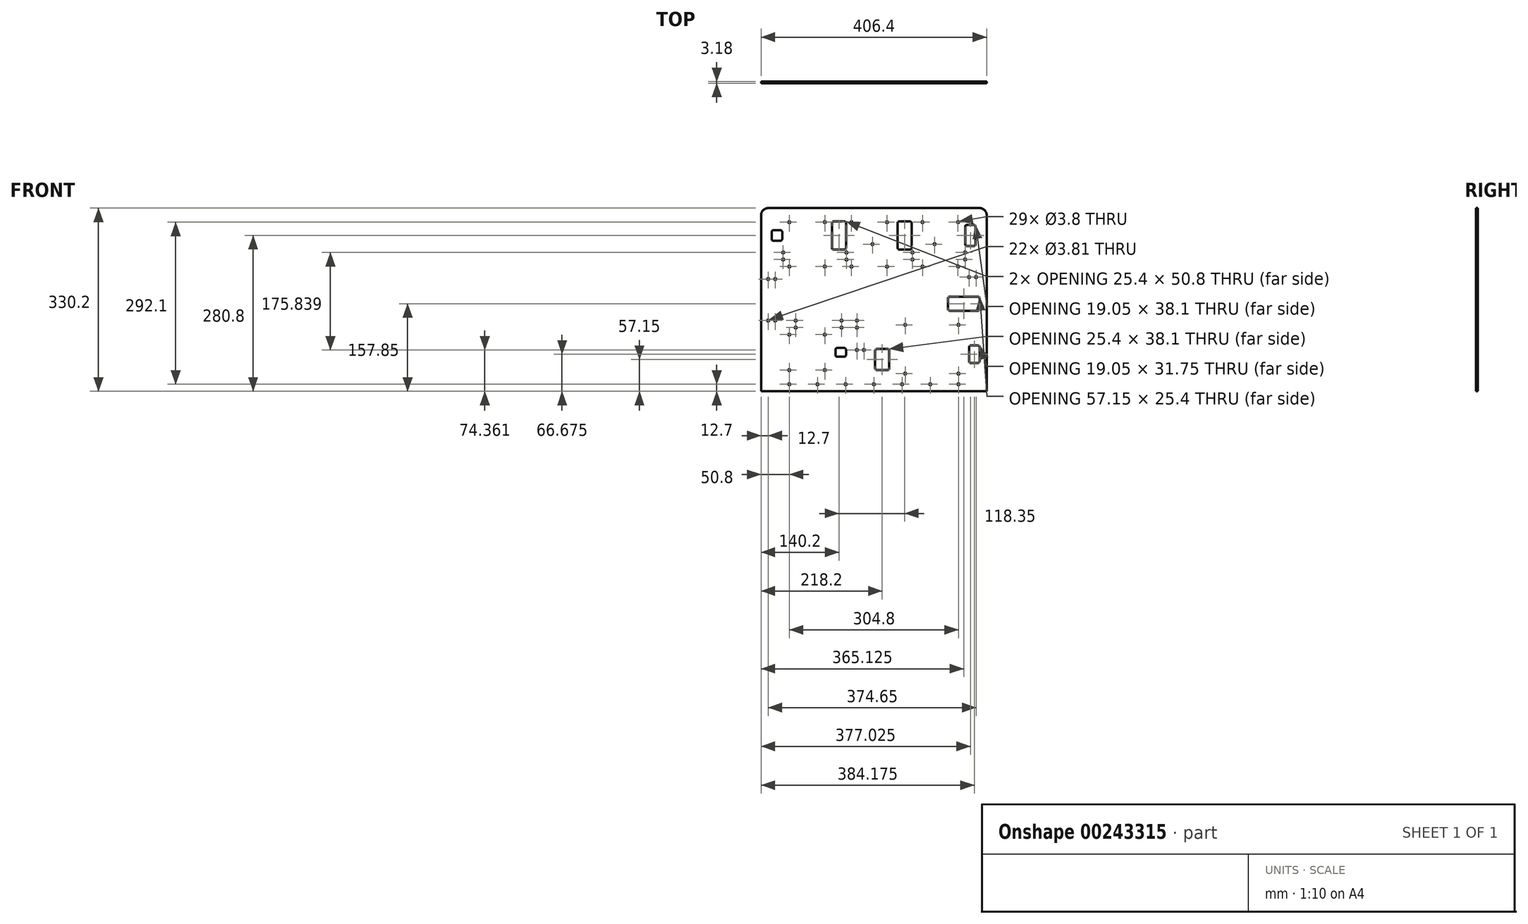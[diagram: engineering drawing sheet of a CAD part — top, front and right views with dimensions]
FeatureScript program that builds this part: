
annotation { "Feature Type Name" : "Feature", "Feature Type Description" : "" }
export const myFeature = defineFeature(function(context is Context, id is Id, definition is map)
    precondition{}
    {
        {
            var Q0;
            Q0=qCreatedBy(makeId("Front.planeOp"),FACE);
            var sketch = newSketch(context, id + "F0", { "sketchPlane" : qUnion([Q0])});
            skLineSegment(sketch, "E0.bottom", {"start": v(-190.5, 165.1) * mm, "end": v(190.5, 165.1) * mm});
            skLineSegment(sketch, "E0.top", {"start": v(-203.2, -165.1) * mm, "end": v(203.2, -165.1) * mm});
            skLineSegment(sketch, "E0.left", {"start": v(-203.2, 152.4) * mm, "end": v(-203.2, -165.1) * mm});
            skLineSegment(sketch, "E0.right", {"start": v(203.2, 152.4) * mm, "end": v(203.2, -165.1) * mm});
            skPoint(sketch, "E0.middle", {"position": v(0, 0) * mm});
            skLineSegment(sketch, "E1", {"start": v(-203.2, -152.4) * mm, "end": v(-152.4, -152.4) * mm, "construction": true});
            skCircle(sketch, "E2", {"center": v(-152.4, -152.4) * mm, "radius": 1.9 * mm});
            skCircle(sketch, "E3.1.0.0", {"center": v(-101.6, -152.4) * mm, "radius": 1.9 * mm});
            skCircle(sketch, "E3.2.0.0", {"center": v(-50.8, -152.4) * mm, "radius": 1.9 * mm});
            skCircle(sketch, "E3.3.0.0", {"center": v(0, -152.4) * mm, "radius": 1.9 * mm});
            skCircle(sketch, "E3.4.0.0", {"center": v(50.8, -152.4) * mm, "radius": 1.9 * mm});
            skCircle(sketch, "E3.5.0.0", {"center": v(101.6, -152.4) * mm, "radius": 1.9 * mm});
            skCircle(sketch, "E3.6.0.0", {"center": v(152.4, -152.4) * mm, "radius": 1.9 * mm});
            skLineSegment(sketch, "E3.direction1", {"start": v(-152.4, -152.4) * mm, "end": v(-101.6, -152.4) * mm, "construction": true});
            skLineSegment(sketch, "E4.bottom", {"start": v(-127, 50.85) * mm, "end": v(127, 50.85) * mm, "construction": true});
            skLineSegment(sketch, "E4.top", {"start": v(-127, -25.35) * mm, "end": v(127, -25.35) * mm, "construction": true});
            skLineSegment(sketch, "E4.left", {"start": v(-127, 50.85) * mm, "end": v(-127, -25.35) * mm, "construction": true});
            skLineSegment(sketch, "E4.right", {"start": v(127, 50.85) * mm, "end": v(127, -25.35) * mm, "construction": true});
            skPoint(sketch, "E4.middle", {"position": v(0, 12.75) * mm});
            skPoint(sketch, "E5.visualSharp", {"position": v(-203.2, 165.1) * mm});
            skArc(sketch, "E5.filletArc", {"start": v(-190.5, 165.1) * mm, "mid": v(-199.48, 161.38) * mm, "end": v(-203.2, 152.4) * mm});
            skPoint(sketch, "E6.visualSharp", {"position": v(203.2, 165.1) * mm});
            skArc(sketch, "E6.filletArc", {"start": v(203.2, 152.4) * mm, "mid": v(199.48, 161.38) * mm, "end": v(190.5, 165.1) * mm});
            skLineSegment(sketch, "E7", {"start": v(-203.2, 139.7) * mm, "end": v(203.2, 139.7) * mm, "construction": true});
            skCircle(sketch, "E8", {"center": v(-152.4, 139.7) * mm, "radius": 1.9 * mm});
            skCircle(sketch, "E9", {"center": v(-136.4, 139.7) * mm, "radius": 1.9 * mm, "construction": true});
            skLineSegment(sketch, "E10", {"start": v(-203.2, 59.7) * mm, "end": v(203.2, 59.7) * mm, "construction": true});
            skLineSegment(sketch, "E11", {"start": v(-203.2, 59.7) * mm, "end": v(-203.2, 139.7) * mm, "construction": true});
            skLineSegment(sketch, "E12", {"start": v(-203.2, 99.7) * mm, "end": v(-136.72, 99.7) * mm, "construction": true});
            skCircle(sketch, "E13.MirrorC", {"center": v(-152.4, 59.7) * mm, "radius": 1.9 * mm});
            skCircle(sketch, "E14.MirrorC", {"center": v(-136.4, 59.7) * mm, "radius": 1.9 * mm, "construction": true});
            skCircle(sketch, "E15.1.0.0", {"center": v(-104.4, 139.7) * mm, "radius": 1.9 * mm, "construction": true});
            skCircle(sketch, "E15.1.0.1", {"center": v(-120.4, 139.7) * mm, "radius": 1.9 * mm, "construction": true});
            skCircle(sketch, "E15.1.0.2", {"center": v(-104.4, 59.7) * mm, "radius": 1.9 * mm, "construction": true});
            skCircle(sketch, "E15.1.0.3", {"center": v(-120.4, 59.7) * mm, "radius": 1.9 * mm, "construction": true});
            skCircle(sketch, "E15.2.0.0", {"center": v(-72.4, 139.7) * mm, "radius": 1.9 * mm, "construction": true});
            skCircle(sketch, "E15.2.0.1", {"center": v(-88.4, 139.7) * mm, "radius": 1.9 * mm});
            skCircle(sketch, "E15.2.0.2", {"center": v(-72.4, 59.7) * mm, "radius": 1.9 * mm, "construction": true});
            skCircle(sketch, "E15.2.0.3", {"center": v(-88.4, 59.7) * mm, "radius": 1.9 * mm});
            skCircle(sketch, "E15.3.0.0", {"center": v(-40.4, 139.7) * mm, "radius": 1.9 * mm});
            skCircle(sketch, "E15.3.0.1", {"center": v(-56.4, 139.7) * mm, "radius": 1.9 * mm, "construction": true});
            skCircle(sketch, "E15.3.0.2", {"center": v(-40.4, 59.7) * mm, "radius": 1.9 * mm});
            skCircle(sketch, "E15.3.0.3", {"center": v(-56.4, 59.7) * mm, "radius": 1.9 * mm, "construction": true});
            skCircle(sketch, "E15.4.0.0", {"center": v(-8.4, 139.7) * mm, "radius": 1.9 * mm, "construction": true});
            skCircle(sketch, "E15.4.0.1", {"center": v(-24.4, 139.7) * mm, "radius": 1.9 * mm, "construction": true});
            skCircle(sketch, "E15.4.0.2", {"center": v(-8.4, 59.7) * mm, "radius": 1.9 * mm, "construction": true});
            skCircle(sketch, "E15.4.0.3", {"center": v(-24.4, 59.7) * mm, "radius": 1.9 * mm, "construction": true});
            skCircle(sketch, "E15.5.0.0", {"center": v(23.6, 139.7) * mm, "radius": 1.9 * mm});
            skCircle(sketch, "E15.5.0.1", {"center": v(7.6, 139.7) * mm, "radius": 1.9 * mm, "construction": true});
            skCircle(sketch, "E15.5.0.2", {"center": v(23.6, 59.7) * mm, "radius": 1.9 * mm});
            skCircle(sketch, "E15.5.0.3", {"center": v(7.6, 59.7) * mm, "radius": 1.9 * mm, "construction": true});
            skCircle(sketch, "E15.6.0.0", {"center": v(55.6, 139.7) * mm, "radius": 1.9 * mm, "construction": true});
            skCircle(sketch, "E15.6.0.1", {"center": v(39.6, 139.7) * mm, "radius": 1.9 * mm, "construction": true});
            skCircle(sketch, "E15.6.0.2", {"center": v(55.6, 59.7) * mm, "radius": 1.9 * mm, "construction": true});
            skCircle(sketch, "E15.6.0.3", {"center": v(39.6, 59.7) * mm, "radius": 1.9 * mm, "construction": true});
            skCircle(sketch, "E15.7.0.0", {"center": v(87.6, 139.7) * mm, "radius": 1.9 * mm});
            skCircle(sketch, "E15.7.0.1", {"center": v(71.6, 139.7) * mm, "radius": 1.9 * mm, "construction": true});
            skCircle(sketch, "E15.7.0.2", {"center": v(87.6, 59.7) * mm, "radius": 1.9 * mm});
            skCircle(sketch, "E15.7.0.3", {"center": v(71.6, 59.7) * mm, "radius": 1.9 * mm, "construction": true});
            skCircle(sketch, "E15.8.0.0", {"center": v(119.6, 139.7) * mm, "radius": 1.9 * mm, "construction": true});
            skCircle(sketch, "E15.8.0.1", {"center": v(103.6, 139.7) * mm, "radius": 1.9 * mm, "construction": true});
            skCircle(sketch, "E15.8.0.2", {"center": v(119.6, 59.7) * mm, "radius": 1.9 * mm, "construction": true});
            skCircle(sketch, "E15.8.0.3", {"center": v(103.6, 59.7) * mm, "radius": 1.9 * mm, "construction": true});
            skCircle(sketch, "E15.9.0.0", {"center": v(151.6, 139.7) * mm, "radius": 1.9 * mm});
            skCircle(sketch, "E15.9.0.1", {"center": v(135.6, 139.7) * mm, "radius": 1.9 * mm, "construction": true});
            skCircle(sketch, "E15.9.0.2", {"center": v(151.6, 59.7) * mm, "radius": 1.9 * mm});
            skCircle(sketch, "E15.9.0.3", {"center": v(135.6, 59.7) * mm, "radius": 1.9 * mm, "construction": true});
            skLineSegment(sketch, "E15.direction1", {"start": v(-136.4, 139.7) * mm, "end": v(-104.4, 139.7) * mm, "construction": true});
            skLineSegment(sketch, "E16", {"start": v(-203.2, -127) * mm, "end": v(0, -127) * mm, "construction": true});
            skCircle(sketch, "E17", {"center": v(-152.4, -127) * mm, "radius": 1.9 * mm});
            skCircle(sketch, "E18", {"center": v(-136.4, -127) * mm, "radius": 1.9 * mm, "construction": true});
            skLineSegment(sketch, "E19", {"start": v(-203.2, -63) * mm, "end": v(0, -63) * mm, "construction": true});
            skLineSegment(sketch, "E20", {"start": v(-203.2, -63) * mm, "end": v(-203.2, -127) * mm, "construction": true});
            skLineSegment(sketch, "E21", {"start": v(-203.2, -95) * mm, "end": v(-174.63, -95) * mm, "construction": true});
            skPoint(sketch, "E21.endSnap0", {"position": v(-203.2, -95) * mm});
            skCircle(sketch, "E22.MirrorC", {"center": v(-136.4, -63) * mm, "radius": 1.9 * mm, "construction": true});
            skCircle(sketch, "E23.MirrorC", {"center": v(-152.4, -63) * mm, "radius": 1.9 * mm});
            skCircle(sketch, "E24.1.0.0", {"center": v(-104.4, -63) * mm, "radius": 1.9 * mm, "construction": true});
            skCircle(sketch, "E24.1.0.1", {"center": v(-120.4, -63) * mm, "radius": 1.9 * mm, "construction": true});
            skCircle(sketch, "E24.1.0.2", {"center": v(-104.4, -127) * mm, "radius": 1.9 * mm, "construction": true});
            skCircle(sketch, "E24.1.0.3", {"center": v(-120.4, -127) * mm, "radius": 1.9 * mm, "construction": true});
            skCircle(sketch, "E24.2.0.0", {"center": v(-72.4, -63) * mm, "radius": 1.9 * mm, "construction": true});
            skCircle(sketch, "E24.2.0.1", {"center": v(-88.4, -63) * mm, "radius": 1.9 * mm});
            skCircle(sketch, "E24.2.0.2", {"center": v(-72.4, -127) * mm, "radius": 1.9 * mm, "construction": true});
            skCircle(sketch, "E24.2.0.3", {"center": v(-88.4, -127) * mm, "radius": 1.9 * mm});
            skLineSegment(sketch, "E24.direction1", {"start": v(-136.4, -63) * mm, "end": v(-104.4, -63) * mm, "construction": true});
            skLineSegment(sketch, "E25", {"start": v(203.2, -133.35) * mm, "end": v(0, -133.35) * mm, "construction": true});
            skLineSegment(sketch, "E26", {"start": v(203.2, -133.35) * mm, "end": v(203.2, -45.35) * mm, "construction": true});
            skLineSegment(sketch, "E27", {"start": v(203.2, -89.35) * mm, "end": v(141.4, -89.35) * mm, "construction": true});
            skLineSegment(sketch, "E28", {"start": v(203.2, -45.35) * mm, "end": v(0, -45.35) * mm, "construction": true});
            skCircle(sketch, "E29", {"center": v(152.4, -133.35) * mm, "radius": 1.9 * mm});
            skCircle(sketch, "E30", {"center": v(136.4, -133.35) * mm, "radius": 1.9 * mm, "construction": true});
            skCircle(sketch, "E31.MirrorC", {"center": v(136.4, -45.35) * mm, "radius": 1.9 * mm, "construction": true});
            skCircle(sketch, "E32.MirrorC", {"center": v(152.4, -45.35) * mm, "radius": 1.9 * mm});
            skCircle(sketch, "E33.1.0.0", {"center": v(104.4, -45.35) * mm, "radius": 1.9 * mm, "construction": true});
            skCircle(sketch, "E33.1.0.1", {"center": v(120.4, -45.35) * mm, "radius": 1.9 * mm, "construction": true});
            skCircle(sketch, "E33.1.0.2", {"center": v(120.4, -133.35) * mm, "radius": 1.9 * mm, "construction": true});
            skCircle(sketch, "E33.1.0.3", {"center": v(104.4, -133.35) * mm, "radius": 1.9 * mm, "construction": true});
            skCircle(sketch, "E33.2.0.0", {"center": v(72.4, -45.35) * mm, "radius": 1.9 * mm, "construction": true});
            skCircle(sketch, "E33.2.0.1", {"center": v(88.4, -45.35) * mm, "radius": 1.9 * mm, "construction": true});
            skCircle(sketch, "E33.2.0.2", {"center": v(88.4, -133.35) * mm, "radius": 1.9 * mm, "construction": true});
            skCircle(sketch, "E33.2.0.3", {"center": v(72.4, -133.35) * mm, "radius": 1.9 * mm, "construction": true});
            skCircle(sketch, "E33.3.0.0", {"center": v(40.4, -45.35) * mm, "radius": 1.9 * mm, "construction": true});
            skCircle(sketch, "E33.3.0.1", {"center": v(56.4, -45.35) * mm, "radius": 1.9 * mm});
            skCircle(sketch, "E33.3.0.2", {"center": v(56.4, -133.35) * mm, "radius": 1.9 * mm});
            skCircle(sketch, "E33.3.0.3", {"center": v(40.4, -133.35) * mm, "radius": 1.9 * mm, "construction": true});
            skLineSegment(sketch, "E33.direction1", {"start": v(136.4, -45.35) * mm, "end": v(104.4, -45.35) * mm, "construction": true});
            skLineSegment(sketch, "E34.bottom", {"start": v(136.52, 5.45) * mm, "end": v(187.33, 5.45) * mm});
            skLineSegment(sketch, "E34.top", {"start": v(136.52, -19.95) * mm, "end": v(187.33, -19.95) * mm});
            skLineSegment(sketch, "E34.left", {"start": v(133.35, 2.28) * mm, "end": v(133.35, -16.78) * mm});
            skLineSegment(sketch, "E34.right", {"start": v(190.5, 2.28) * mm, "end": v(190.5, -16.78) * mm});
            skPoint(sketch, "E34.middle", {"position": v(161.92, -7.25) * mm});
            skPoint(sketch, "E35.visualSharp", {"position": v(133.35, 5.45) * mm});
            skArc(sketch, "E35.filletArc", {"start": v(136.52, 5.45) * mm, "mid": v(134.28, 4.52) * mm, "end": v(133.35, 2.28) * mm});
            skPoint(sketch, "E36.visualSharp", {"position": v(190.5, 5.45) * mm});
            skArc(sketch, "E36.filletArc", {"start": v(190.5, 2.28) * mm, "mid": v(189.57, 4.52) * mm, "end": v(187.33, 5.45) * mm});
            skPoint(sketch, "E37.visualSharp", {"position": v(190.5, -19.95) * mm});
            skArc(sketch, "E37.filletArc", {"start": v(187.33, -19.95) * mm, "mid": v(189.57, -19.02) * mm, "end": v(190.5, -16.78) * mm});
            skPoint(sketch, "E38.visualSharp", {"position": v(133.35, -19.95) * mm});
            skArc(sketch, "E38.filletArc", {"start": v(133.35, -16.78) * mm, "mid": v(134.28, -19.02) * mm, "end": v(136.52, -19.95) * mm});
            skLineSegment(sketch, "E39.bottom", {"start": v(174.63, -82.55) * mm, "end": v(187.33, -82.55) * mm});
            skLineSegment(sketch, "E39.top", {"start": v(174.63, -114.3) * mm, "end": v(187.33, -114.3) * mm});
            skLineSegment(sketch, "E39.left", {"start": v(171.45, -85.73) * mm, "end": v(171.45, -111.13) * mm});
            skLineSegment(sketch, "E39.right", {"start": v(190.5, -85.73) * mm, "end": v(190.5, -111.13) * mm});
            skPoint(sketch, "E39.middle", {"position": v(180.98, -98.43) * mm});
            skPoint(sketch, "E40.visualSharp", {"position": v(171.45, -82.55) * mm});
            skArc(sketch, "E40.filletArc", {"start": v(174.63, -82.55) * mm, "mid": v(172.38, -83.48) * mm, "end": v(171.45, -85.73) * mm});
            skPoint(sketch, "E41.visualSharp", {"position": v(190.5, -82.55) * mm});
            skArc(sketch, "E41.filletArc", {"start": v(190.5, -85.73) * mm, "mid": v(189.57, -83.48) * mm, "end": v(187.33, -82.55) * mm});
            skPoint(sketch, "E42.visualSharp", {"position": v(171.45, -114.3) * mm});
            skArc(sketch, "E42.filletArc", {"start": v(171.45, -111.13) * mm, "mid": v(172.38, -113.37) * mm, "end": v(174.63, -114.3) * mm});
            skPoint(sketch, "E43.visualSharp", {"position": v(190.5, -114.3) * mm});
            skArc(sketch, "E43.filletArc", {"start": v(187.33, -114.3) * mm, "mid": v(189.57, -113.37) * mm, "end": v(190.5, -111.13) * mm});
            skLineSegment(sketch, "E44.bottom", {"start": v(5.47, -88.9) * mm, "end": v(24.52, -88.9) * mm});
            skLineSegment(sketch, "E44.top", {"start": v(5.47, -127) * mm, "end": v(24.52, -127) * mm});
            skLineSegment(sketch, "E44.left", {"start": v(2.3, -92.08) * mm, "end": v(2.3, -123.83) * mm});
            skLineSegment(sketch, "E44.right", {"start": v(27.7, -92.08) * mm, "end": v(27.7, -123.83) * mm});
            skPoint(sketch, "E44.middle", {"position": v(15, -107.95) * mm});
            skPoint(sketch, "E45.visualSharp", {"position": v(27.7, -88.9) * mm});
            skArc(sketch, "E45.filletArc", {"start": v(27.7, -92.08) * mm, "mid": v(26.77, -89.83) * mm, "end": v(24.52, -88.9) * mm});
            skPoint(sketch, "E46.visualSharp", {"position": v(2.3, -88.9) * mm});
            skArc(sketch, "E46.filletArc", {"start": v(5.47, -88.9) * mm, "mid": v(3.23, -89.83) * mm, "end": v(2.3, -92.08) * mm});
            skPoint(sketch, "E47.visualSharp", {"position": v(27.7, -127) * mm});
            skArc(sketch, "E47.filletArc", {"start": v(24.52, -127) * mm, "mid": v(26.77, -126.07) * mm, "end": v(27.7, -123.83) * mm});
            skPoint(sketch, "E48.visualSharp", {"position": v(2.3, -127) * mm});
            skArc(sketch, "E48.filletArc", {"start": v(2.3, -123.83) * mm, "mid": v(3.23, -126.07) * mm, "end": v(5.47, -127) * mm});
            skLineSegment(sketch, "E49.bottom", {"start": v(-66.18, -87.06) * mm, "end": v(-53.48, -87.06) * mm});
            skLineSegment(sketch, "E49.top", {"start": v(-66.18, -102.94) * mm, "end": v(-53.48, -102.94) * mm});
            skLineSegment(sketch, "E49.left", {"start": v(-69.35, -90.24) * mm, "end": v(-69.35, -99.76) * mm});
            skLineSegment(sketch, "E49.right", {"start": v(-50.3, -90.24) * mm, "end": v(-50.3, -99.76) * mm});
            skPoint(sketch, "E49.middle", {"position": v(-59.83, -95) * mm});
            skPoint(sketch, "E50.visualSharp", {"position": v(-69.35, -87.06) * mm});
            skArc(sketch, "E50.filletArc", {"start": v(-66.18, -87.06) * mm, "mid": v(-68.42, -88) * mm, "end": v(-69.35, -90.24) * mm});
            skPoint(sketch, "E51.visualSharp", {"position": v(-50.3, -102.94) * mm});
            skArc(sketch, "E51.filletArc", {"start": v(-53.48, -102.94) * mm, "mid": v(-51.23, -102) * mm, "end": v(-50.3, -99.76) * mm});
            skPoint(sketch, "E52.visualSharp", {"position": v(-50.3, -87.06) * mm});
            skArc(sketch, "E52.filletArc", {"start": v(-50.3, -90.24) * mm, "mid": v(-51.23, -88) * mm, "end": v(-53.48, -87.06) * mm});
            skPoint(sketch, "E53.visualSharp", {"position": v(-69.35, -102.94) * mm});
            skArc(sketch, "E53.filletArc", {"start": v(-69.35, -99.76) * mm, "mid": v(-68.42, -102) * mm, "end": v(-66.18, -102.94) * mm});
            skLineSegment(sketch, "E54.bottom", {"start": v(-180.98, 125.22) * mm, "end": v(-168.28, 125.22) * mm});
            skLineSegment(sketch, "E54.top", {"start": v(-180.98, 106.17) * mm, "end": v(-168.28, 106.17) * mm});
            skLineSegment(sketch, "E54.left", {"start": v(-184.15, 122.05) * mm, "end": v(-184.15, 109.35) * mm});
            skLineSegment(sketch, "E54.right", {"start": v(-165.1, 122.05) * mm, "end": v(-165.1, 109.35) * mm});
            skPoint(sketch, "E54.middle", {"position": v(-174.63, 115.7) * mm});
            skPoint(sketch, "E55.visualSharp", {"position": v(-165.1, 125.22) * mm});
            skArc(sketch, "E55.filletArc", {"start": v(-165.1, 122.05) * mm, "mid": v(-166.03, 124.3) * mm, "end": v(-168.28, 125.22) * mm});
            skPoint(sketch, "E56.visualSharp", {"position": v(-165.1, 106.17) * mm});
            skArc(sketch, "E56.filletArc", {"start": v(-168.28, 106.17) * mm, "mid": v(-166.03, 107.1) * mm, "end": v(-165.1, 109.35) * mm});
            skPoint(sketch, "E57.visualSharp", {"position": v(-184.15, 106.17) * mm});
            skArc(sketch, "E57.filletArc", {"start": v(-184.15, 109.35) * mm, "mid": v(-183.22, 107.1) * mm, "end": v(-180.98, 106.17) * mm});
            skPoint(sketch, "E58.visualSharp", {"position": v(-184.15, 125.22) * mm});
            skArc(sketch, "E58.filletArc", {"start": v(-180.98, 125.22) * mm, "mid": v(-183.22, 124.3) * mm, "end": v(-184.15, 122.05) * mm});
            skLineSegment(sketch, "E59.bottom", {"start": v(-72.53, 141.1) * mm, "end": v(-53.48, 141.1) * mm});
            skLineSegment(sketch, "E59.top", {"start": v(-72.53, 90.3) * mm, "end": v(-53.48, 90.3) * mm});
            skLineSegment(sketch, "E59.left", {"start": v(-75.7, 137.93) * mm, "end": v(-75.7, 93.48) * mm});
            skLineSegment(sketch, "E59.right", {"start": v(-50.3, 137.93) * mm, "end": v(-50.3, 93.48) * mm});
            skPoint(sketch, "E59.middle", {"position": v(-63, 115.7) * mm});
            skPoint(sketch, "E60.visualSharp", {"position": v(-75.7, 141.1) * mm});
            skArc(sketch, "E60.filletArc", {"start": v(-72.53, 141.1) * mm, "mid": v(-74.77, 140.17) * mm, "end": v(-75.7, 137.93) * mm});
            skPoint(sketch, "E61.visualSharp", {"position": v(-50.3, 141.1) * mm});
            skArc(sketch, "E61.filletArc", {"start": v(-50.3, 137.93) * mm, "mid": v(-51.23, 140.17) * mm, "end": v(-53.48, 141.1) * mm});
            skPoint(sketch, "E62.visualSharp", {"position": v(-50.3, 90.3) * mm});
            skArc(sketch, "E62.filletArc", {"start": v(-53.48, 90.3) * mm, "mid": v(-51.23, 91.23) * mm, "end": v(-50.3, 93.48) * mm});
            skPoint(sketch, "E63.visualSharp", {"position": v(-75.7, 90.3) * mm});
            skArc(sketch, "E63.filletArc", {"start": v(-75.7, 93.48) * mm, "mid": v(-74.77, 91.23) * mm, "end": v(-72.53, 90.3) * mm});
            skLineSegment(sketch, "E64.bottom", {"start": v(45.82, 141.1) * mm, "end": v(64.88, 141.1) * mm});
            skLineSegment(sketch, "E64.top", {"start": v(45.82, 90.3) * mm, "end": v(64.88, 90.3) * mm});
            skLineSegment(sketch, "E64.left", {"start": v(42.65, 137.93) * mm, "end": v(42.65, 93.48) * mm});
            skLineSegment(sketch, "E64.right", {"start": v(68.05, 137.93) * mm, "end": v(68.05, 93.48) * mm});
            skPoint(sketch, "E64.middle", {"position": v(55.35, 115.7) * mm});
            skPoint(sketch, "E65.visualSharp", {"position": v(42.65, 141.1) * mm});
            skArc(sketch, "E65.filletArc", {"start": v(45.82, 141.1) * mm, "mid": v(43.58, 140.17) * mm, "end": v(42.65, 137.93) * mm});
            skPoint(sketch, "E66.visualSharp", {"position": v(68.05, 141.1) * mm});
            skArc(sketch, "E66.filletArc", {"start": v(68.05, 137.93) * mm, "mid": v(67.12, 140.17) * mm, "end": v(64.88, 141.1) * mm});
            skPoint(sketch, "E67.visualSharp", {"position": v(68.05, 90.3) * mm});
            skArc(sketch, "E67.filletArc", {"start": v(64.88, 90.3) * mm, "mid": v(67.12, 91.23) * mm, "end": v(68.05, 93.48) * mm});
            skPoint(sketch, "E68.visualSharp", {"position": v(42.65, 90.3) * mm});
            skArc(sketch, "E68.filletArc", {"start": v(42.65, 93.48) * mm, "mid": v(43.58, 91.23) * mm, "end": v(45.82, 90.3) * mm});
            skPoint(sketch, "E69.middle.positionSnap0", {"position": v(55.35, 90.3) * mm});
            skPoint(sketch, "E69.centerSnap0", {"position": v(55.35, 90.3) * mm});
            skLineSegment(sketch, "E70.bottom", {"start": v(167.47, 134.75) * mm, "end": v(180.18, 134.75) * mm});
            skLineSegment(sketch, "E70.top", {"start": v(167.47, 96.65) * mm, "end": v(180.18, 96.65) * mm});
            skLineSegment(sketch, "E70.left", {"start": v(164.3, 131.58) * mm, "end": v(164.3, 99.83) * mm});
            skLineSegment(sketch, "E70.right", {"start": v(183.35, 131.58) * mm, "end": v(183.35, 99.82) * mm});
            skPoint(sketch, "E70.middle", {"position": v(173.83, 115.7) * mm});
            skLineSegment(sketch, "E71", {"start": v(203.2, 115.7) * mm, "end": v(-203.2, 115.7) * mm, "construction": true});
            skPoint(sketch, "E71.startSnap0", {"position": v(183.35, 115.7) * mm});
            skPoint(sketch, "E72.visualSharp", {"position": v(164.3, 134.75) * mm});
            skArc(sketch, "E72.filletArc", {"start": v(167.47, 134.75) * mm, "mid": v(165.23, 133.82) * mm, "end": v(164.3, 131.58) * mm});
            skPoint(sketch, "E73.visualSharp", {"position": v(164.3, 96.65) * mm});
            skArc(sketch, "E73.filletArc", {"start": v(164.3, 99.83) * mm, "mid": v(165.23, 97.58) * mm, "end": v(167.47, 96.65) * mm});
            skPoint(sketch, "E74.visualSharp", {"position": v(183.35, 134.75) * mm});
            skArc(sketch, "E74.filletArc", {"start": v(183.35, 131.58) * mm, "mid": v(182.42, 133.82) * mm, "end": v(180.18, 134.75) * mm});
            skPoint(sketch, "E75.visualSharp", {"position": v(183.35, 96.65) * mm});
            skArc(sketch, "E75.filletArc", {"start": v(180.18, 96.65) * mm, "mid": v(182.42, 97.58) * mm, "end": v(183.35, 99.82) * mm});
            skLineSegment(sketch, "E76", {"start": v(-203.2, 72.4) * mm, "end": v(203.2, 72.4) * mm, "construction": true});
            skLineSegment(sketch, "E77", {"start": v(203.2, 85.1) * mm, "end": v(-203.2, 85.1) * mm, "construction": true});
            skCircle(sketch, "E78", {"center": v(-163.5, 85.1) * mm, "radius": 1.9 * mm});
            skCircle(sketch, "E79", {"center": v(-49.36, 85.1) * mm, "radius": 1.9 * mm});
            skCircle(sketch, "E80", {"center": v(69.51, 85.1) * mm, "radius": 1.9 * mm});
            skCircle(sketch, "E81", {"center": v(164.38, 85.1) * mm, "radius": 1.9 * mm});
            skCircle(sketch, "E82", {"center": v(184.15, 40.65) * mm, "radius": 1.9 * mm});
            skLineSegment(sketch, "E83", {"start": v(203.2, 72.4) * mm, "end": v(203.2, 85.1) * mm, "construction": true});
            skLineSegment(sketch, "E84", {"start": v(203.2, 78.75) * mm, "end": v(-203.2, 78.75) * mm, "construction": true});
            skCircle(sketch, "E85.MirrorC", {"center": v(-49.36, 72.4) * mm, "radius": 1.9 * mm});
            skCircle(sketch, "E86.MirrorC", {"center": v(69.51, 72.4) * mm, "radius": 1.9 * mm});
            skCircle(sketch, "E87.MirrorC", {"center": v(164.38, 72.4) * mm, "radius": 1.9 * mm});
            skCircle(sketch, "E88.MirrorC", {"center": v(-163.5, 72.4) * mm, "radius": 1.9 * mm});
            skCircle(sketch, "E89", {"center": v(171.45, 40.65) * mm, "radius": 1.9 * mm});
            skCircle(sketch, "E90", {"center": v(-190.5, 37.18) * mm, "radius": 1.9 * mm});
            skCircle(sketch, "E91", {"center": v(-190.5, -37.6) * mm, "radius": 1.9 * mm});
            skCircle(sketch, "E92", {"center": v(-140.88, -37.6) * mm, "radius": 1.9 * mm});
            skCircle(sketch, "E93", {"center": v(-58.2, -37.6) * mm, "radius": 1.9 * mm});
            skCircle(sketch, "E94", {"center": v(-30.49, -37.6) * mm, "radius": 1.9 * mm});
            skCircle(sketch, "E95", {"center": v(-30.49, -90.74) * mm, "radius": 1.9 * mm});
            skLineSegment(sketch, "E96", {"start": v(-184.15, 37.18) * mm, "end": v(-184.15, -63) * mm, "construction": true});
            skCircle(sketch, "E97.MirrorC", {"center": v(-177.8, 37.18) * mm, "radius": 1.9 * mm});
            skCircle(sketch, "E98.MirrorC", {"center": v(-177.8, -37.6) * mm, "radius": 1.9 * mm});
            skLineSegment(sketch, "E99", {"start": v(-143.16, -43.95) * mm, "end": v(-22.01, -43.95) * mm, "construction": true});
            skCircle(sketch, "E100.MirrorC", {"center": v(-58.2, -50.3) * mm, "radius": 1.9 * mm});
            skCircle(sketch, "E101.MirrorC", {"center": v(-140.88, -50.3) * mm, "radius": 1.9 * mm});
            skCircle(sketch, "E102.MirrorC", {"center": v(-30.49, -50.3) * mm, "radius": 1.9 * mm});
            skLineSegment(sketch, "E103", {"start": v(-24.14, -70.06) * mm, "end": v(-24.14, -104.8) * mm, "construction": true});
            skCircle(sketch, "E104.MirrorC", {"center": v(-17.79, -90.74) * mm, "radius": 1.9 * mm});
            skCircle(sketch, "E105", {"center": v(-66.54, 180.04) * mm, "radius": 1.9 * mm});
            skCircle(sketch, "E106.MirrorC", {"center": v(-66.54, 100.04) * mm, "radius": 1.9 * mm});
            skCircle(sketch, "E107.2.0.3", {"center": v(-2.54, 100.04) * mm, "radius": 1.9 * mm});
            skCircle(sketch, "E107.3.0.0", {"center": v(45.46, 180.04) * mm, "radius": 1.9 * mm});
            skCircle(sketch, "E107.3.0.2", {"center": v(45.46, 100.04) * mm, "radius": 1.9 * mm});
            skCircle(sketch, "E107.5.0.0", {"center": v(109.46, 180.04) * mm, "radius": 1.9 * mm});
            skCircle(sketch, "E107.5.0.2", {"center": v(109.46, 100.04) * mm, "radius": 1.9 * mm});
            skCircle(sketch, "E107.7.0.0", {"center": v(173.46, 180.04) * mm, "radius": 1.9 * mm});
            skCircle(sketch, "E107.7.0.2", {"center": v(173.46, 100.04) * mm, "radius": 1.9 * mm});
            skCircle(sketch, "E107.9.0.0", {"center": v(237.46, 180.04) * mm, "radius": 1.9 * mm});
            skCircle(sketch, "E107.9.0.2", {"center": v(237.46, 100.04) * mm, "radius": 1.9 * mm});
            skSolve(sketch);
        }
        {
            var Q0;
            Q0=makeQuery(id+"F0.imprint","IMPRINT",FACE,{"disambiguationData":[TD([[makeQuery(id+"F0.imprint","IMPRINT",EDGE,{"derivedFrom":sQuery(id+"F0.wireOp",EDGE,"E0.bottom")}),-1.0]])]});
            var Q1;
            Q1 = qConstructionFilter(qBodyType(qCreatedBy(id + "F0" ,EDGE), BodyType.WIRE), ConstructionObject.NO);
            extrude(context, id + "F1", {"entities" : qUnion([Q0]), "surfaceEntities" : qUnion([Q1]), "depth" : 3.17 * mm});
        }
    });
